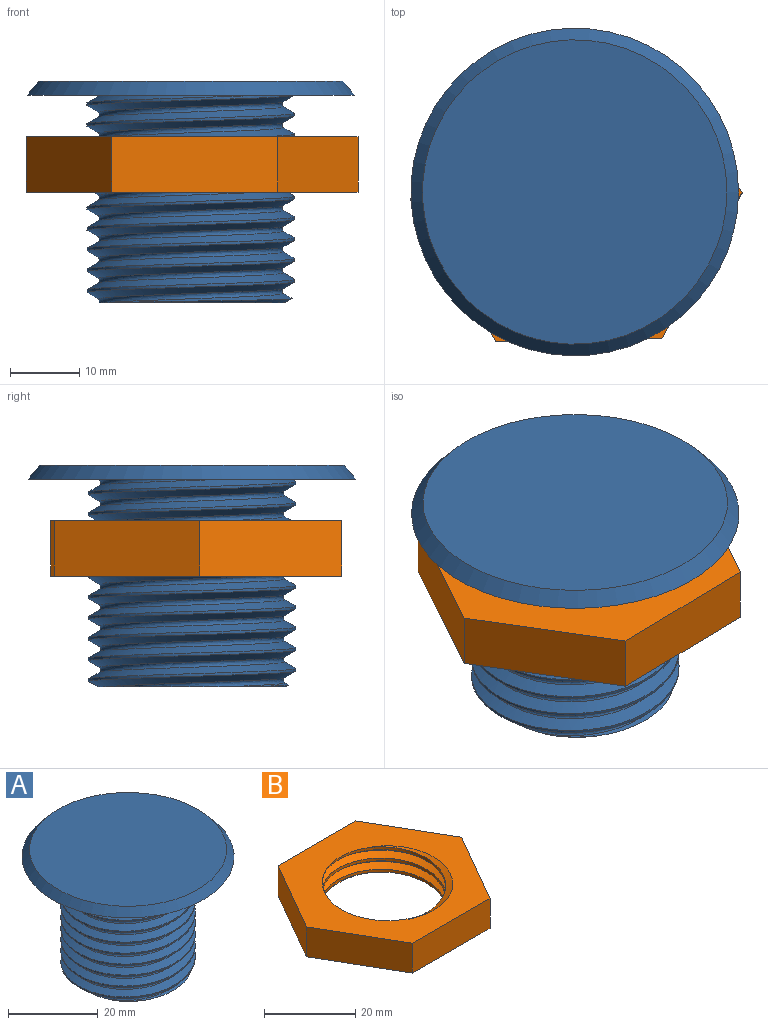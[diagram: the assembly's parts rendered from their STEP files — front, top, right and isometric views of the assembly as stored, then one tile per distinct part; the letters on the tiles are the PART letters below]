
ASSEMBLY  parts=2 mates=1
PART A: 15 faces, bbox 48.2x48.2x34 mm
  f0: cylinder r=15mm len=30mm, axis (0,0,1), area 260.6mm2, adj f1,f12,f13,f14
  f1: plane 39.84x39.84mm, normal (0,0,-1), area 572.3mm2, adj f0,f5,f11,f12,f13
  f2: plane 27.14x26.89mm, normal (0,0,-1), area 187.2mm2, adj f3,f11,f12,f13,f14
  f3: cylinder r=11mm len=28mm, axis (0,0,1), area 1935.2mm2, adj f2,f4
  f4: plane 22x22mm, normal (0,0,-1), area 380.1mm2, adj f3
  f5: cylinder r=19.5mm len=39mm, axis (0,0,-1), area 61.3mm2, adj f1,f7
  f6: cylinder r=20.5mm len=41mm, axis (0,0,-1), area 64.4mm2, adj f7,f10
  f7: plane 41x41mm, normal (0,0,-1), area 125.7mm2, adj f5,f6
  f8: plane 44x44mm, normal (0,0,1), area 1520.5mm2, adj f9
  f9: cone r=22mm half-angle=40deg, axis (0,0,-1), area 374.7mm2, adj f8,f10
  f10: plane 47.36x47.36mm, normal (0,0,-1), area 441.1mm2, adj f6,f9
  f11: bspline ~32.25x30.89mm, area 701.2mm2, adj f1,f2,f12,f13
  f12: bspline ~34.64x32.44mm, area 1648.2mm2, adj f0,f1,f2,f11,f14
  f13: bspline ~34.64x31.44mm, area 1652.5mm2, adj f0,f1,f2,f11,f14
  f14: cone r=15mm half-angle=63.4deg, axis (0,0,1), area 61.4mm2, adj f0,f2,f12,f13
PART B: 12 faces, bbox 48.9x42.5x11.3 mm
  f0: plane 20.78x12mm, normal (0.87,0.5,0), area 192mm2, adj f1,f5,f6,f7
  f1: plane 24x8mm, normal (0,1,0), area 192mm2, adj f0,f2,f6,f7
  f2: plane 20.78x12mm, normal (-0.87,0.5,0), area 192mm2, adj f1,f3,f6,f7
  f3: plane 20.78x12mm, normal (-0.87,-0.5,0), area 192mm2, adj f2,f4,f6,f7
  f4: plane 24x8mm, normal (0,-1,0), area 192mm2, adj f3,f5,f6,f7
  f5: plane 20.78x12mm, normal (0.87,-0.5,0), area 192mm2, adj f0,f4,f6,f7
  f6: plane 48.91x42.47mm, normal (0,0,1), area 860.1mm2, adj f0,f1,f2,f3,f4,f5,f8,f9
  f7: plane 48.91x42.47mm, normal (0,0,-1), area 860.1mm2, adj f0,f1,f2,f3,f4,f5,f8,f9
  f8: bspline ~34.93x30.25mm, area 449.8mm2, adj f6,f7,f10,f11
  f9: bspline ~34.93x30.25mm, area 449.7mm2, adj f6,f7,f10,f11
  f10: bspline ~35.24x30.52mm, area 110.6mm2, adj f6,f7,f8,f9
  f11: cylinder r=13.5mm len=27mm, axis (0,0,1), area 169.9mm2, adj f6,f7,f8,f9
PLACE A t=(-13.52,-12.05,10.86)mm fixed
PLACE B rot(axis=(0,0,-1),118.8deg) t=(-13.34,-12.67,-3.15)mm
MATE cylindrical B.f7 <-> A.f0  axis (0,0,-1) through (-13.52,-12.05,-3.15)mm
